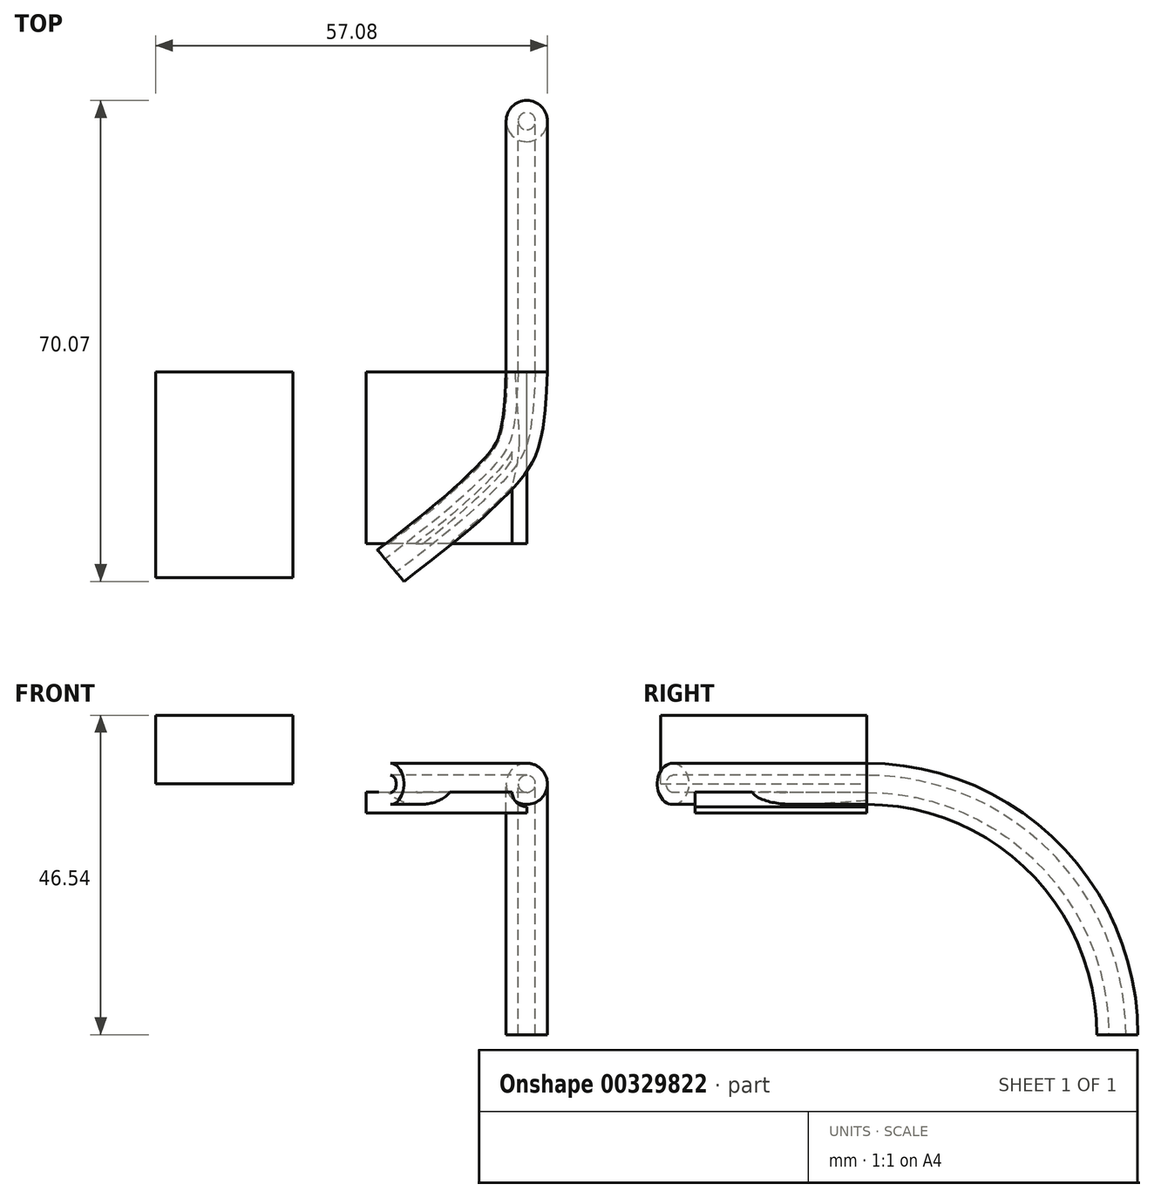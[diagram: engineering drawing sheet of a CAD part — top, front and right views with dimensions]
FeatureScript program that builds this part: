
annotation { "Feature Type Name" : "Feature", "Feature Type Description" : "" }
export const myFeature = defineFeature(function(context is Context, id is Id, definition is map)
    precondition{}
    {
        {
            var Q0;
            Q0=qCreatedBy(makeId("Top.planeOp"),FACE);
            var sketch = newSketch(context, id + "F0", { "sketchPlane" : qUnion([Q0])});
            skFitSpline(sketch, "E0", {"points": [v(0, 0) * mm, v(-2.5, -12.86) * mm, v(-6.97, -17.66) * mm, v(-19.84, -28.23) * mm], "startDerivative": vector(-3.13, -70.42) * mm, "endDerivative": vector(-62.94, -48.06) * mm});
            skSolve(sketch);
        }
        {
            var Q0;
            Q0=qCreatedBy(makeId("Front.planeOp"),FACE);
            var sketch = newSketch(context, id + "F1", { "sketchPlane" : qUnion([Q0])});
            skCircle(sketch, "E1", {"center": v(0, 0) * mm, "radius": 1.25 * mm});
            skCircle(sketch, "E2", {"center": v(0, 0) * mm, "radius": 3 * mm});
            skSolve(sketch);
        }
        {
            var Q0;
            Q0 = qSketchRegion(id + "F1", true);
            var Q1;
            Q1=sQuery(id+"F0.wireOp",EDGE,"E0");
            sweep(context, id + "F2", {"profiles" : qUnion([Q0]), "path" : qUnion([Q1])});
        }
        {
            var Q0;
            Q0=qCreatedBy(makeId("Front.planeOp"),FACE);
            var sketch = newSketch(context, id + "F3", { "sketchPlane" : qUnion([Q0])});
            skArc(sketch, "E3", {"start": v(-2.12, -1.2) * mm, "mid": v(-1.5, -2.7) * mm, "end": v(0, -3.33) * mm});
            skLineSegment(sketch, "E4", {"start": v(0, -3.33) * mm, "end": v(0, -4.24) * mm});
            skLineSegment(sketch, "E5", {"start": v(0, -4.24) * mm, "end": v(-23.42, -4.24) * mm});
            skLineSegment(sketch, "E6", {"start": v(-23.42, -4.24) * mm, "end": v(-23.42, -1.2) * mm});
            skLineSegment(sketch, "E7", {"start": v(-23.42, -1.2) * mm, "end": v(-2.12, -1.2) * mm});
            skSolve(sketch);
        }
        {
            var Q0;
            Q0=makeQuery(id+"F3.imprint","IMPRINT",FACE,{"disambiguationData":[TD([[makeQuery(id+"F3.imprint","IMPRINT",EDGE,{"derivedFrom":sQuery(id+"F3.wireOp",EDGE,"E3")}),-1.0]])]});
            extrude(context, id + "F4", {"entities" : qUnion([Q0]), "operationType" : NewBodyOperationType.ADD, "depth" : 25 * mm});
        }
        {
            var Q0;
            Q0=qCreatedBy(makeId("Right.planeOp"),FACE);
            var sketch = newSketch(context, id + "F5", { "sketchPlane" : qUnion([Q0])});
            skArc(sketch, "E8", {"start": v(36.54, -36.54) * mm, "mid": v(25.84, -10.7) * mm, "end": v(0, 0) * mm});
            skSolve(sketch);
        }
        {
            var Q0;
            Q0 = qSketchRegion(id + "F1", true);
            var Q1;
            Q1=sQuery(id+"F5.wireOp",EDGE,"E8");
            sweep(context, id + "F6", {"operationType" : NewBodyOperationType.ADD, "profiles" : qUnion([Q0]), "path" : qUnion([Q1])});
        }
        {
            var Q0;
            Q0=qCreatedBy(makeId("Front.planeOp"),FACE);
            var sketch = newSketch(context, id + "F7", { "sketchPlane" : qUnion([Q0])});
            skLineSegment(sketch, "E9.bottom", {"start": v(-54.08, 0) * mm, "end": v(-34.08, 0) * mm});
            skLineSegment(sketch, "E9.top", {"start": v(-54.08, 10) * mm, "end": v(-34.08, 10) * mm});
            skLineSegment(sketch, "E9.left", {"start": v(-54.08, 0) * mm, "end": v(-54.08, 10) * mm});
            skLineSegment(sketch, "E9.right", {"start": v(-34.08, 0) * mm, "end": v(-34.08, 10) * mm});
            skSolve(sketch);
        }
        {
            var Q0;
            Q0=makeQuery(id+"F7.imprint","IMPRINT",FACE,{"disambiguationData":[TD([[makeQuery(id+"F7.imprint","IMPRINT",EDGE,{"derivedFrom":sQuery(id+"F7.wireOp",EDGE,"E9.bottom")}),1.0]])]});
            extrude(context, id + "F8", {"entities" : qUnion([Q0]), "depth" : 30 * mm});
        }
    });
